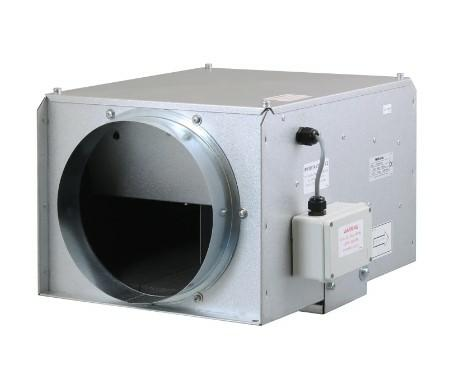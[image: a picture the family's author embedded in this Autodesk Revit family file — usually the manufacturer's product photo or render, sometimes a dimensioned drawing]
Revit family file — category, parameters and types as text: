
# Revit family: CADS_Vent-Axia_MechEquip_Fan_ACQ - EXTRACT
name_source: partatom
category: Mechanical Equipment
units: mm (PartAtom-declared; Revit-internal decimal feet)

## family parameters
Classification = None
Cut with Voids When Loaded = No
Host = Face
OmniClass Number = 23.75.35.17.11
OmniClass Title = Fans for Air Ductwork
Part Type = Normal
Room Calculation Point = No
Round Connector Dimension = Use Diameter
Shared = No

## types (10) — shared parameters
AirflowRateRange = 0.0 L/s
AssemblyPlace = UNKNOWN
AssetType = FIXED
Default Elevation = 1219 mm
DurationUnit = Year
ExteriorInsulation = No
Fitting Type = Ignore
GrossWeight = 0.00 kg
HasProtectiveEarth = No
IsExtendedWarranty = No
ManufacturerAddress = Fleming Way
Crawley 
RH10 9YX
Quantity = 1
RatedCurrent = 0 A
RatedVoltage = 0 V
Status = New
Type Image = CADS_Vent-Axia_MechEquip_Fan_ACQ.jpg
WorkingPressure = 0.0 Pa
zero-valued in all types: CADS_Index, CADS_Usage, ExpectedServiceLife, H, NumberOfPoles, OverallLength, SpigotLength, W

## per-type parameters (varying)
| type | EBHoffset | EBVoffset | L | ModelReference | NominalDiameter | NominalHeight | NominalLength | NominalWidth | OutOffset | Size | SpigotCLHeight |
| ACQ10012D | 110 mm  [stored 0.360892 ft] | 55 mm  [stored 0.180446 ft] | 360 mm | ACOUSTIC BOX FAN, 100 DIA SPIGOTS | 100 mm  [stored 0.328084 ft] | 190 mm | 400 mm | 310 mm  [stored 1.01706 ft] | 62 mm | 400mm x310mm x190mm | 94 mm |
| ACQ12512D | 109 mm | 49 mm | 360 mm | ACOUSTIC BOX FAN, 125 DIA SPIGOTS | 125 mm  [stored 0.410105 ft] | 190 mm | 400 mm | 310 mm  [stored 1.01706 ft] | 63 mm | 400mm x310mm x190mm | 94 mm |
| ACQ15012D | 92 mm | 94 mm | 360 mm | ACOUSTIC BOX FAN, 150 DIA SPIGOTS | 150 mm | 190 mm | 400 mm | 310 mm  [stored 1.01706 ft] | 50 mm | 400mm x310mm x190mm | 94 mm |
| ACQ16012D | 109 mm | 49 mm | 360 mm | ACOUSTIC BOX FAN, 160 DIA SPIGOTS | 160 mm  [stored 0.524934 ft] | 190 mm | 400 mm | 310 mm  [stored 1.01706 ft] | 45 mm  [stored 0.147638 ft] | 400mm x310mm x190mm | 94 mm |
| ACQ20012D | 93 mm | 92 mm | 415 mm | ACOUSTIC BOX FAN, 200 DIA SPIGOTS | 200 mm  [stored 0.656168 ft] | 285 mm  [stored 0.935039 ft] | 455 mm | 364 mm  [stored 1.19423 ft] | 55 mm  [stored 0.180446 ft] | 455mm x364mm x285mm | 140 mm |
| ACQ25012D | 92 mm | 92 mm | 415 mm | ACOUSTIC BOX FAN, 250 DIA SPIGOTS | 250 mm  [stored 0.82021 ft] | 285 mm  [stored 0.935039 ft] | 455 mm | 364 mm  [stored 1.19423 ft] | 30 mm  [stored 0.0984252 ft] | 455mm x364mm x285mm | 141 mm |
| ACQ31512LD | 90 mm | 123 mm | 415 mm | ACOUSTIC BOX FAN, 315 DIA SPIGOTS | 315 mm  [stored 1.03346 ft] | 348 mm  [stored 1.14173 ft] | 455 mm | 404 mm | 20 mm  [stored 0.0656168 ft] | 455mm x404mm x348mm | 173 mm |
| ACQ31514HD | 106 mm | 257 mm | 690 mm | ACOUSTIC BOX FAN, 315 DIA SPIGOTS | 315 mm  [stored 1.03346 ft] | 456 mm | 730 mm | 572 mm | 43 mm | 730mm x572mm x456mm | 227 mm |
| ACQ40014D | 106 mm | 257 mm | 690 mm | ACOUSTIC BOX FAN, 400 DIA SPIGOTS | 400 mm | 456 mm | 730 mm | 572 mm | 45 mm  [stored 0.147638 ft] | 730mm x572mm x456mm | 226 mm |
| ACQ50014D | 240 mm  [stored 0.787402 ft] | 392 mm | 878 mm | ACOUSTIC BOX FAN, 500 DIA SPIGOTS | 500 mm | 575 mm | 918 mm | 769 mm | 60 mm | 918mm x769mm x575mm | 286 mm |

note: column(s) folded — value = type name in every type: ModelNumber

note: [stored X ft] marks values corroborated as IEEE doubles in the binary element streams (Revit-internal decimal feet)

## geometry (parser evidence)
native form markers: Sweep x5
no freeform markers — native parametric forms only
